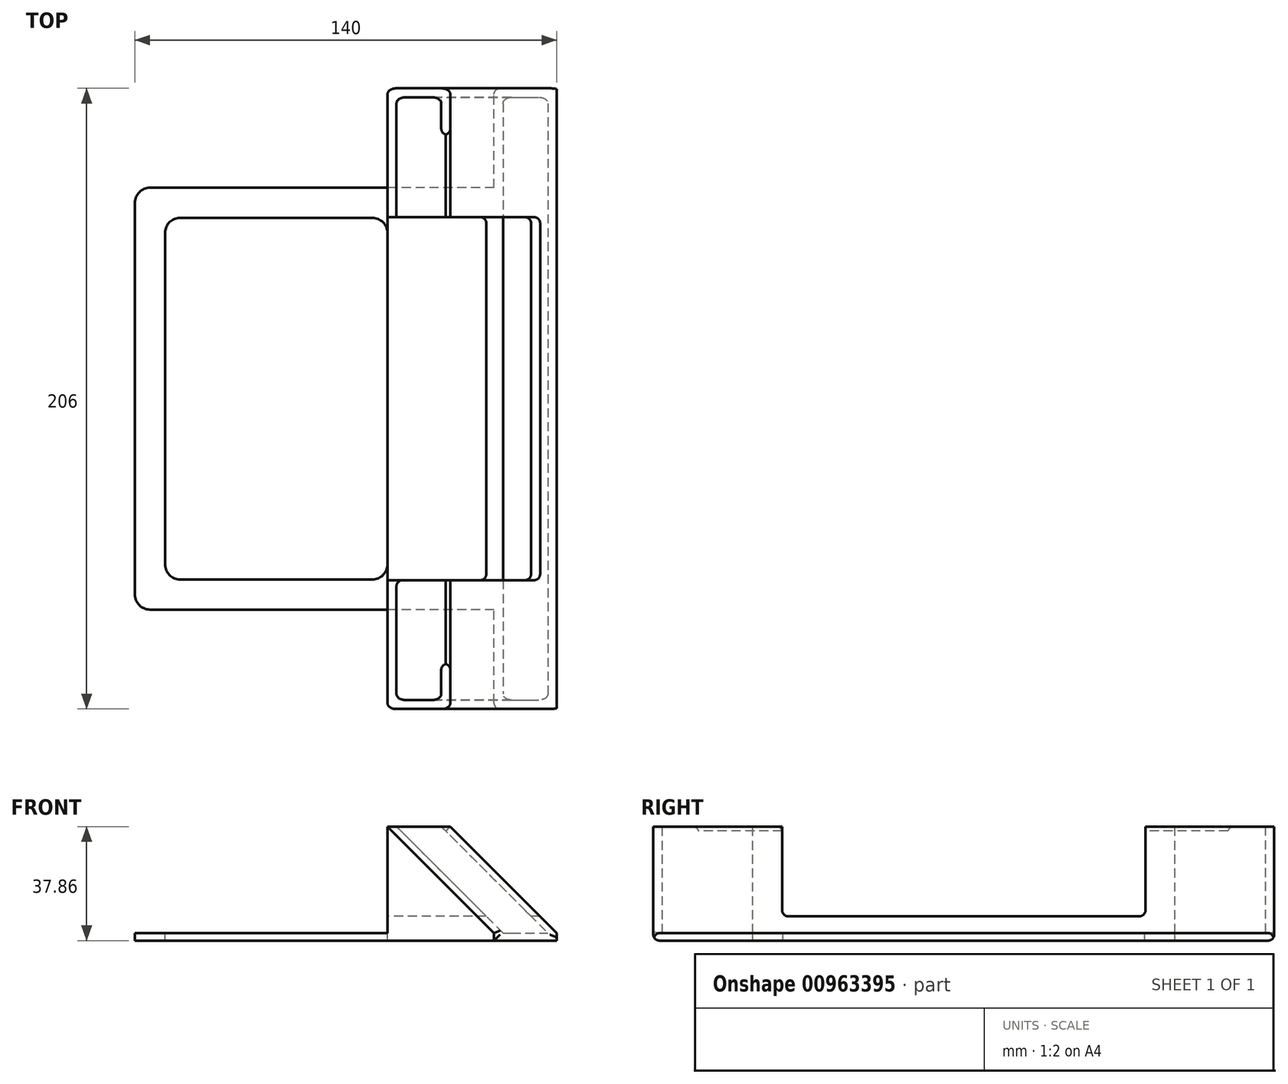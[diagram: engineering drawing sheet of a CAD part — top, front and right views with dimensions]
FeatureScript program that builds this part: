
annotation { "Feature Type Name" : "Feature", "Feature Type Description" : "" }
export const myFeature = defineFeature(function(context is Context, id is Id, definition is map)
    precondition{}
    {
        {
            var Q0;
            Q0=qCreatedBy(makeId("Front.planeOp"),FACE);
            var sketch = newSketch(context, id + "F0", { "sketchPlane" : qUnion([Q0])});
            skLineSegment(sketch, "E0", {"start": v(0, 0) * mm, "end": v(-140, 0) * mm});
            skLineSegment(sketch, "E1", {"start": v(-140, 0) * mm, "end": v(-140, 2.5) * mm});
            skLineSegment(sketch, "E2", {"start": v(-140, 2.5) * mm, "end": v(0, 2.5) * mm});
            skLineSegment(sketch, "E3", {"start": v(0, 2.5) * mm, "end": v(0, 0) * mm});
            skLineSegment(sketch, "E4", {"start": v(0, 2.5) * mm, "end": v(-35.36, 37.86) * mm});
            skLineSegment(sketch, "E5", {"start": v(-17.85, 2.5) * mm, "end": v(-53.2, 37.86) * mm});
            skLineSegment(sketch, "E6", {"start": v(-20.85, 2.5) * mm, "end": v(-56.2, 37.86) * mm});
            skLineSegment(sketch, "E7", {"start": v(-56.2, 37.86) * mm, "end": v(-53.2, 37.86) * mm});
            skLineSegment(sketch, "E8", {"start": v(-56.2, 37.86) * mm, "end": v(-56.2, 2.5) * mm});
            skLineSegment(sketch, "E9", {"start": v(-56.2, 2.5) * mm, "end": v(-53.2, 2.5) * mm});
            skLineSegment(sketch, "E10", {"start": v(-53.2, 2.5) * mm, "end": v(-53.2, 34.86) * mm});
            skLineSegment(sketch, "E11", {"start": v(0, 2.5) * mm, "end": v(-3, 2.5) * mm});
            skLineSegment(sketch, "E12", {"start": v(-35.36, 37.86) * mm, "end": v(-38.36, 37.86) * mm});
            skLineSegment(sketch, "E13", {"start": v(-38.36, 37.86) * mm, "end": v(-3, 2.5) * mm});
            skLineSegment(sketch, "E14", {"start": v(-20.85, 2.5) * mm, "end": v(-20.85, 0) * mm});
            skLineSegment(sketch, "E15", {"start": v(-38.36, 37.86) * mm, "end": v(-53.2, 37.86) * mm});
            skSolve(sketch);
        }
        {
            var Q0;
            {var subQ3=sQuery(id+"F0.wireOp",EDGE,"E1");Q0=makeQuery(id+"F0.imprint","IMPRINT",FACE,{"disambiguationData":[TD([[makeQuery(id+"F0.imprint","IMPRINT",EDGE,{"derivedFrom":subQ3}),-1.0]])]});}
            extrude(context, id + "F1", {"entities" : qUnion([Q0]), "endBound" : BoundingType.SYMMETRIC, "depth" : 140 * mm, "offsetDistance" : 25 * mm});
        }
        {
            var Q0;
            {var subQ0=sQuery(id+"F0.wireOp",EDGE,"E3");Q0=makeQuery(id+"F0.imprint","IMPRINT",FACE,{"disambiguationData":[TD([[makeQuery(id+"F0.imprint","IMPRINT",EDGE,{"derivedFrom":subQ0}),-1.0]])]});}
            var Q1;
            {var subQ3=sQuery(id+"F0.wireOp",EDGE,"E5");Q1=makeQuery(id+"F0.imprint","IMPRINT",FACE,{"disambiguationData":[TD([[makeQuery(id+"F0.imprint","IMPRINT",EDGE,{"derivedFrom":subQ3}),1.0]])]});}
            var Q2;
            Q2=makeQuery(id+"F0.imprint","IMPRINT",FACE,{"disambiguationData":[TD([[makeQuery(id+"F0.imprint","IMPRINT",EDGE,{"derivedFrom":sQuery(id+"F0.wireOp",EDGE,"E4")}),1.0]])]});
            var Q3;
            {var subQ2=sQuery(id+"F0.wireOp",EDGE,"E5");Q3=makeQuery(id+"F0.imprint","IMPRINT",FACE,{"disambiguationData":[TD([[makeQuery(id+"F0.imprint","IMPRINT",EDGE,{"derivedFrom":subQ2}),-1.0]])]});}
            extrude(context, id + "F2", {"entities" : qUnion([Q0, Q1, Q2, Q3]), "operationType" : NewBodyOperationType.ADD, "endBound" : BoundingType.SYMMETRIC, "depth" : 206 * mm, "offsetDistance" : 25 * mm});
        }
        {
            var Q0;
            {var subQ2=sQuery(id+"F0.wireOp",EDGE,"E5");Q0=makeQuery(id+"F0.imprint","IMPRINT",FACE,{"disambiguationData":[TD([[makeQuery(id+"F0.imprint","IMPRINT",EDGE,{"derivedFrom":subQ2}),-1.0]])]});}
            extrude(context, id + "F3", {"entities" : qUnion([Q0]), "operationType" : NewBodyOperationType.REMOVE, "endBound" : BoundingType.SYMMETRIC, "oppositeDirection" : true, "depth" : 200 * mm, "offsetDistance" : 25 * mm});
        }
        {
            var Q0;
            Q0=makeQuery(id+"F2.opExtrude","SWEPT_FACE",FACE,{"disambiguationData":[OSD([sQuery(id+"F0.wireOp",EDGE,"E4")])]});
            var sketch = newSketch(context, id + "F4", { "sketchPlane" : qUnion([Q0])});
            skLineSegment(sketch, "E16.top", {"start": v(-88, 6.77) * mm, "end": v(88, 6.77) * mm});
            skLineSegment(sketch, "E16.left", {"start": v(-88, 51.77) * mm, "end": v(-88, 6.77) * mm});
            skLineSegment(sketch, "E16.right", {"start": v(88, 51.06) * mm, "end": v(88, 6.77) * mm});
            skLineSegment(sketch, "E17.bottom", {"start": v(-88, 6.77) * mm, "end": v(87.63, 6.77) * mm});
            skLineSegment(sketch, "E17.top", {"start": v(-88, 70.67) * mm, "end": v(87.63, 70.67) * mm});
            skLineSegment(sketch, "E17.left", {"start": v(-88, 6.77) * mm, "end": v(-88, 70.67) * mm});
            skLineSegment(sketch, "E17.right", {"start": v(87.63, 6.77) * mm, "end": v(87.63, 70.67) * mm});
            skSolve(sketch);
        }
        {
            var Q0;
            {var subQ0=sQuery(id+"F4.wireOp",EDGE,"E17.top");Q0=makeQuery(id+"F4.imprint","IMPRINT",FACE,{"disambiguationData":[TD([[makeQuery(id+"F4.imprint","IMPRINT",EDGE,{"derivedFrom":subQ0}),-1.0]])]});}
            var Q1;
            {var subQ0=sQuery(id+"F4.wireOp",EDGE,"E17.bottom");Q1=makeQuery(id+"F4.imprint","IMPRINT",FACE,{"disambiguationData":[TD([[makeQuery(id+"F4.imprint","IMPRINT",EDGE,{"derivedFrom":subQ0}),1.0]])]});}
            extrude(context, id + "F5", {"entities" : qUnion([Q0, Q1]), "operationType" : NewBodyOperationType.REMOVE, "oppositeDirection" : true, "depth" : 5 * mm, "offsetDistance" : 25 * mm});
        }
        {
            var Q0;
            {var subQ3=sQuery(id+"F0.wireOp",EDGE,"E10");Q0=makeQuery(id+"F0.imprint","IMPRINT",FACE,{"disambiguationData":[TD([[makeQuery(id+"F0.imprint","IMPRINT",EDGE,{"derivedFrom":subQ3}),-1.0]])]});}
            var Q1;
            {var subQ0=sQuery(id+"F0.wireOp",EDGE,"E8");Q1=makeQuery(id+"F0.imprint","IMPRINT",FACE,{"disambiguationData":[TD([[makeQuery(id+"F0.imprint","IMPRINT",EDGE,{"derivedFrom":subQ0}),1.0]])]});}
            extrude(context, id + "F6", {"entities" : qUnion([Q0, Q1]), "operationType" : NewBodyOperationType.ADD, "endBound" : BoundingType.SYMMETRIC, "depth" : 140 * mm, "offsetDistance" : 25 * mm});
        }
        {
            var Q0;
            Q0=makeQuery(id+"F6.opExtrude","SWEPT_FACE",FACE,{"disambiguationData":[OSD([sQuery(id+"F0.wireOp",EDGE,"E8")])]});
            var sketch = newSketch(context, id + "F7", { "sketchPlane" : qUnion([Q0])});
            skLineSegment(sketch, "E18.bottom", {"start": v(-60.25, 8.06) * mm, "end": v(0, 8.06) * mm});
            skLineSegment(sketch, "E18.top", {"start": v(-60.25, 64.25) * mm, "end": v(0, 64.25) * mm});
            skLineSegment(sketch, "E18.left", {"start": v(-60.25, 8.06) * mm, "end": v(-60.25, 64.25) * mm});
            skLineSegment(sketch, "E18.right", {"start": v(0, 8.06) * mm, "end": v(0, 64.25) * mm});
            skLineSegment(sketch, "E19.MirrorCS", {"start": v(60.25, 64.25) * mm, "end": v(0, 64.25) * mm});
            skLineSegment(sketch, "E20.MirrorCS", {"start": v(60.25, 8.06) * mm, "end": v(60.25, 64.25) * mm});
            skLineSegment(sketch, "E21.MirrorCS", {"start": v(60.25, 8.06) * mm, "end": v(0, 8.06) * mm});
            skSolve(sketch);
        }
        {
            var Q0;
            {var subQ0=sQuery(id+"F7.wireOp",EDGE,"E18.bottom");Q0=makeQuery(id+"F7.imprint","IMPRINT",FACE,{"disambiguationData":[TD([[makeQuery(id+"F7.imprint","IMPRINT",EDGE,{"derivedFrom":subQ0}),1.0]])]});}
            var Q1;
            {var subQ0=sQuery(id+"F7.wireOp",EDGE,"E21.MirrorCS");Q1=makeQuery(id+"F7.imprint","IMPRINT",FACE,{"disambiguationData":[TD([[makeQuery(id+"F7.imprint","IMPRINT",EDGE,{"derivedFrom":subQ0}),-1.0]])]});}
            extrude(context, id + "F8", {"entities" : qUnion([Q0, Q1]), "operationType" : NewBodyOperationType.REMOVE, "oppositeDirection" : true, "depth" : 77 * mm, "offsetDistance" : 25 * mm});
        }
        {
            var Q0;
            Q0=makeQuery(id+"F1.opExtrude","SWEPT_FACE",FACE,{"disambiguationData":[OSD([sQuery(id+"F0.wireOp",EDGE,"E2"),sQuery(id+"F0.wireOp",EDGE,"E9")])]});
            var sketch = newSketch(context, id + "F9", { "sketchPlane" : qUnion([Q0])});
            skLineSegment(sketch, "E22", {"start": v(-140, 60) * mm, "end": v(-56.2, 60) * mm});
            skLineSegment(sketch, "E23.MirrorCS", {"start": v(-140, -60) * mm, "end": v(-56.2, -60) * mm});
            skLineSegment(sketch, "E24", {"start": v(-130, 60) * mm, "end": v(-130, -60) * mm});
            skSolve(sketch);
        }
        {
            var Q0;
            {var subQ3=sQuery(id+"F9.wireOp",EDGE,"E24");Q0=makeQuery(id+"F9.imprint","IMPRINT",FACE,{"disambiguationData":[TD([[makeQuery(id+"F9.imprint","IMPRINT",EDGE,{"derivedFrom":subQ3}),1.0]])]});}
            extrude(context, id + "F10", {"entities" : qUnion([Q0]), "operationType" : NewBodyOperationType.REMOVE, "oppositeDirection" : true, "depth" : 25 * mm, "offsetDistance" : 25 * mm});
        }
        {
            var Q0;
            {var subQ0=sQuery(id+"F0.wireOp",EDGE,"E8");var subQ1=sQuery(id+"F0.wireOp",EDGE,"E9");var subQ2=sQuery(id+"F0.wireOp",EDGE,"E2");Q0=makeQuery(id+"F10.boolean.opBoolean","SPLIT",EDGE,{"disambiguationData":[TD([makeQuery(id+"F10.opExtrude","SWEPT_FACE",FACE,{"disambiguationData":[OSD([sQuery(id+"F9.wireOp",EDGE,"E22")])]})])],"derivedFrom":makeQuery(id+"F6.opExtrude","SWEPT_EDGE",EDGE,{"disambiguationData":[OSD([subQ2,subQ0,subQ1])]})});}
            var Q1;
            {var subQ0=sQuery(id+"F0.wireOp",EDGE,"E8");var subQ1=sQuery(id+"F0.wireOp",EDGE,"E9");var subQ2=sQuery(id+"F0.wireOp",EDGE,"E2");Q1=makeQuery(id+"F10.boolean.opBoolean","SPLIT",EDGE,{"disambiguationData":[TD([makeQuery(id+"F10.opExtrude","SWEPT_FACE",FACE,{"disambiguationData":[OSD([sQuery(id+"F9.wireOp",EDGE,"E23.MirrorCS")])]})])],"derivedFrom":makeQuery(id+"F6.opExtrude","SWEPT_EDGE",EDGE,{"disambiguationData":[OSD([subQ2,subQ0,subQ1])]})});}
            var Q2;
            Q2=makeQuery(id+"F1.opExtrude","CAP_EDGE",EDGE,{"disambiguationData":[OSD([sQuery(id+"F0.wireOp",EDGE,"E1")])],"isStart":false});
            var Q3;
            Q3=makeQuery(id+"F1.opExtrude","CAP_EDGE",EDGE,{"disambiguationData":[OSD([sQuery(id+"F0.wireOp",EDGE,"E1")])],"isStart":true});
            var Q4;
            Q4=makeQuery(id+"F10.boolean.opBoolean","COPY",EDGE,{"derivedFrom":makeQuery(id+"F10.opExtrude","SWEPT_EDGE",EDGE,{"disambiguationData":[OSD([sQuery(id+"F9.wireOp",EDGE,"E23.MirrorCS"),sQuery(id+"F9.wireOp",EDGE,"E24")])]})});
            var Q5;
            Q5=makeQuery(id+"F10.boolean.opBoolean","COPY",EDGE,{"derivedFrom":makeQuery(id+"F10.opExtrude","SWEPT_EDGE",EDGE,{"disambiguationData":[OSD([sQuery(id+"F9.wireOp",EDGE,"E22"),sQuery(id+"F9.wireOp",EDGE,"E24")])]})});
            var Q6;
            Q6=makeQuery(id+"F10.boolean.opBoolean","COPY",EDGE,{"derivedFrom":makeQuery(id+"F10.opExtrude","SWEPT_EDGE",EDGE,{"disambiguationData":[OSD([sQuery(id+"F0.wireOp",EDGE,"E2"),sQuery(id+"F0.wireOp",EDGE,"E8"),sQuery(id+"F0.wireOp",EDGE,"E9"),sQuery(id+"F9.wireOp",EDGE,"E22")])]})});
            var Q7;
            Q7=makeQuery(id+"F10.boolean.opBoolean","COPY",EDGE,{"derivedFrom":makeQuery(id+"F10.opExtrude","SWEPT_EDGE",EDGE,{"disambiguationData":[OSD([sQuery(id+"F0.wireOp",EDGE,"E2"),sQuery(id+"F0.wireOp",EDGE,"E8"),sQuery(id+"F0.wireOp",EDGE,"E9"),sQuery(id+"F9.wireOp",EDGE,"E23.MirrorCS")])]})});
            fillet(context, id + "F11", {"entities" : qUnion([Q0, Q1, Q2, Q3, Q4, Q5, Q6, Q7]), "radius" : 5 * mm, "tangentPropagation" : true, "allowEdgeOverflow" : false});
        }
        {
            var Q0;
            Q0=makeQuery(id+"F3.boolean.opBoolean","COPY",EDGE,{"derivedFrom":makeQuery(id+"F3.opExtrude","CAP_EDGE",EDGE,{"disambiguationData":[OSD([sQuery(id+"F0.wireOp",EDGE,"E13")])],"isStart":true})});
            var Q1;
            Q1=makeQuery(id+"F3.boolean.opBoolean","COPY",EDGE,{"derivedFrom":makeQuery(id+"F3.opExtrude","CAP_EDGE",EDGE,{"disambiguationData":[OSD([sQuery(id+"F0.wireOp",EDGE,"E5")])],"isStart":true})});
            var Q2;
            Q2=makeQuery(id+"F2.opExtrude","CAP_EDGE",EDGE,{"disambiguationData":[OSD([sQuery(id+"F0.wireOp",EDGE,"E4")])],"isStart":false});
            var Q3;
            Q3=makeQuery(id+"F2.opExtrude","CAP_EDGE",EDGE,{"disambiguationData":[OSD([sQuery(id+"F0.wireOp",EDGE,"E6")])],"isStart":false});
            var Q4;
            Q4=makeQuery(id+"F3.boolean.opBoolean","COPY",EDGE,{"derivedFrom":makeQuery(id+"F3.opExtrude","CAP_EDGE",EDGE,{"disambiguationData":[OSD([sQuery(id+"F0.wireOp",EDGE,"E5")])],"isStart":false})});
            var Q5;
            Q5=makeQuery(id+"F3.boolean.opBoolean","COPY",EDGE,{"derivedFrom":makeQuery(id+"F3.opExtrude","CAP_EDGE",EDGE,{"disambiguationData":[OSD([sQuery(id+"F0.wireOp",EDGE,"E13")])],"isStart":false})});
            var Q6;
            Q6=makeQuery(id+"F2.opExtrude","CAP_EDGE",EDGE,{"disambiguationData":[OSD([sQuery(id+"F0.wireOp",EDGE,"E6")])],"isStart":true});
            var Q7;
            Q7=makeQuery(id+"F2.opExtrude","CAP_EDGE",EDGE,{"disambiguationData":[OSD([sQuery(id+"F0.wireOp",EDGE,"E4")])],"isStart":true});
            var Q8;
            Q8=makeQuery(id+"F5.boolean.opBoolean","COPY",EDGE,{"derivedFrom":makeQuery(id+"F5.opExtrude","SWEPT_EDGE",EDGE,{"disambiguationData":[OSD([sQuery(id+"F4.wireOp",EDGE,"E16.top"),sQuery(id+"F4.wireOp",EDGE,"E17.bottom"),sQuery(id+"F4.wireOp",EDGE,"E17.right")])]})});
            var Q9;
            Q9=makeQuery(id+"F5.boolean.opBoolean","COPY",EDGE,{"derivedFrom":makeQuery(id+"F5.opExtrude","SWEPT_EDGE",EDGE,{"disambiguationData":[OSD([sQuery(id+"F4.wireOp",EDGE,"E17.bottom"),sQuery(id+"F4.wireOp",EDGE,"E17.left")])]})});
            var Q10;
            Q10=makeQuery(id+"F5.boolean.opBoolean","INTERSECT",EDGE,{"derivedFrom":[makeQuery(id+"F2.opExtrude","SWEPT_FACE",FACE,{"disambiguationData":[OSD([sQuery(id+"F0.wireOp",EDGE,"E7"),sQuery(id+"F0.wireOp",EDGE,"E12"),sQuery(id+"F0.wireOp",EDGE,"l2zjkzjx-cgva-teKH-sMzs-ATQaICRggI6S")])]}),makeQuery(id+"F5.opExtrude","SWEPT_FACE",FACE,{"disambiguationData":[OSD([sQuery(id+"F4.wireOp",EDGE,"E17.left")])]})]});
            var Q11;
            Q11=makeQuery(id+"F5.boolean.opBoolean","INTERSECT",EDGE,{"derivedFrom":[makeQuery(id+"F2.opExtrude","SWEPT_FACE",FACE,{"disambiguationData":[OSD([sQuery(id+"F0.wireOp",EDGE,"E7"),sQuery(id+"F0.wireOp",EDGE,"E12"),sQuery(id+"F0.wireOp",EDGE,"l2zjkzjx-cgva-teKH-sMzs-ATQaICRggI6S")])]}),makeQuery(id+"F5.opExtrude","SWEPT_FACE",FACE,{"disambiguationData":[OSD([sQuery(id+"F4.wireOp",EDGE,"E17.right")])]})]});
            var Q12;
            Q12=makeQuery(id+"F8.boolean.opBoolean","COPY",EDGE,{"derivedFrom":makeQuery(id+"F8.opExtrude","SWEPT_EDGE",EDGE,{"disambiguationData":[OSD([sQuery(id+"F0.wireOp",EDGE,"E6"),sQuery(id+"F0.wireOp",EDGE,"E7"),sQuery(id+"F0.wireOp",EDGE,"E8"),sQuery(id+"F7.wireOp",EDGE,"E18.left")])]})});
            var Q13;
            Q13=makeQuery(id+"F8.boolean.opBoolean","COPY",EDGE,{"derivedFrom":makeQuery(id+"F8.opExtrude","SWEPT_EDGE",EDGE,{"disambiguationData":[OSD([sQuery(id+"F0.wireOp",EDGE,"E6"),sQuery(id+"F0.wireOp",EDGE,"E7"),sQuery(id+"F0.wireOp",EDGE,"E8"),sQuery(id+"F7.wireOp",EDGE,"E20.MirrorCS")])]})});
            var Q14;
            Q14=makeQuery(id+"F8.boolean.opBoolean","COPY",EDGE,{"derivedFrom":makeQuery(id+"F8.opExtrude","SWEPT_EDGE",EDGE,{"disambiguationData":[OSD([sQuery(id+"F7.wireOp",EDGE,"E20.MirrorCS"),sQuery(id+"F7.wireOp",EDGE,"E21.MirrorCS")])]})});
            var Q15;
            Q15=makeQuery(id+"F8.boolean.opBoolean","COPY",EDGE,{"derivedFrom":makeQuery(id+"F8.opExtrude","SWEPT_EDGE",EDGE,{"disambiguationData":[OSD([sQuery(id+"F7.wireOp",EDGE,"E18.bottom"),sQuery(id+"F7.wireOp",EDGE,"E18.left")])]})});
            var Q16;
            Q16=makeQuery(id+"F2.opExtrude","CAP_EDGE",EDGE,{"disambiguationData":[OSD([sQuery(id+"F0.wireOp",EDGE,"E14")])],"isStart":true});
            var Q17;
            Q17=makeQuery(id+"F2.opExtrude","CAP_EDGE",EDGE,{"disambiguationData":[OSD([sQuery(id+"F0.wireOp",EDGE,"E14")])],"isStart":false});
            var Q18;
            Q18=makeQuery(id+"F2.opExtrude","CAP_EDGE",EDGE,{"disambiguationData":[OSD([sQuery(id+"F0.wireOp",EDGE,"E0")])],"isStart":false});
            var Q19;
            Q19=makeQuery(id+"F2.opExtrude","CAP_EDGE",EDGE,{"disambiguationData":[OSD([sQuery(id+"F0.wireOp",EDGE,"E0")])],"isStart":true});
            fillet(context, id + "F12", {"entities" : qUnion([Q0, Q1, Q2, Q3, Q4, Q5, Q6, Q7, Q8, Q9, Q10, Q11, Q12, Q13, Q14, Q15, Q16, Q17, Q18, Q19]), "radius" : 2 * mm, "tangentPropagation" : true, "allowEdgeOverflow" : false});
        }
    });
